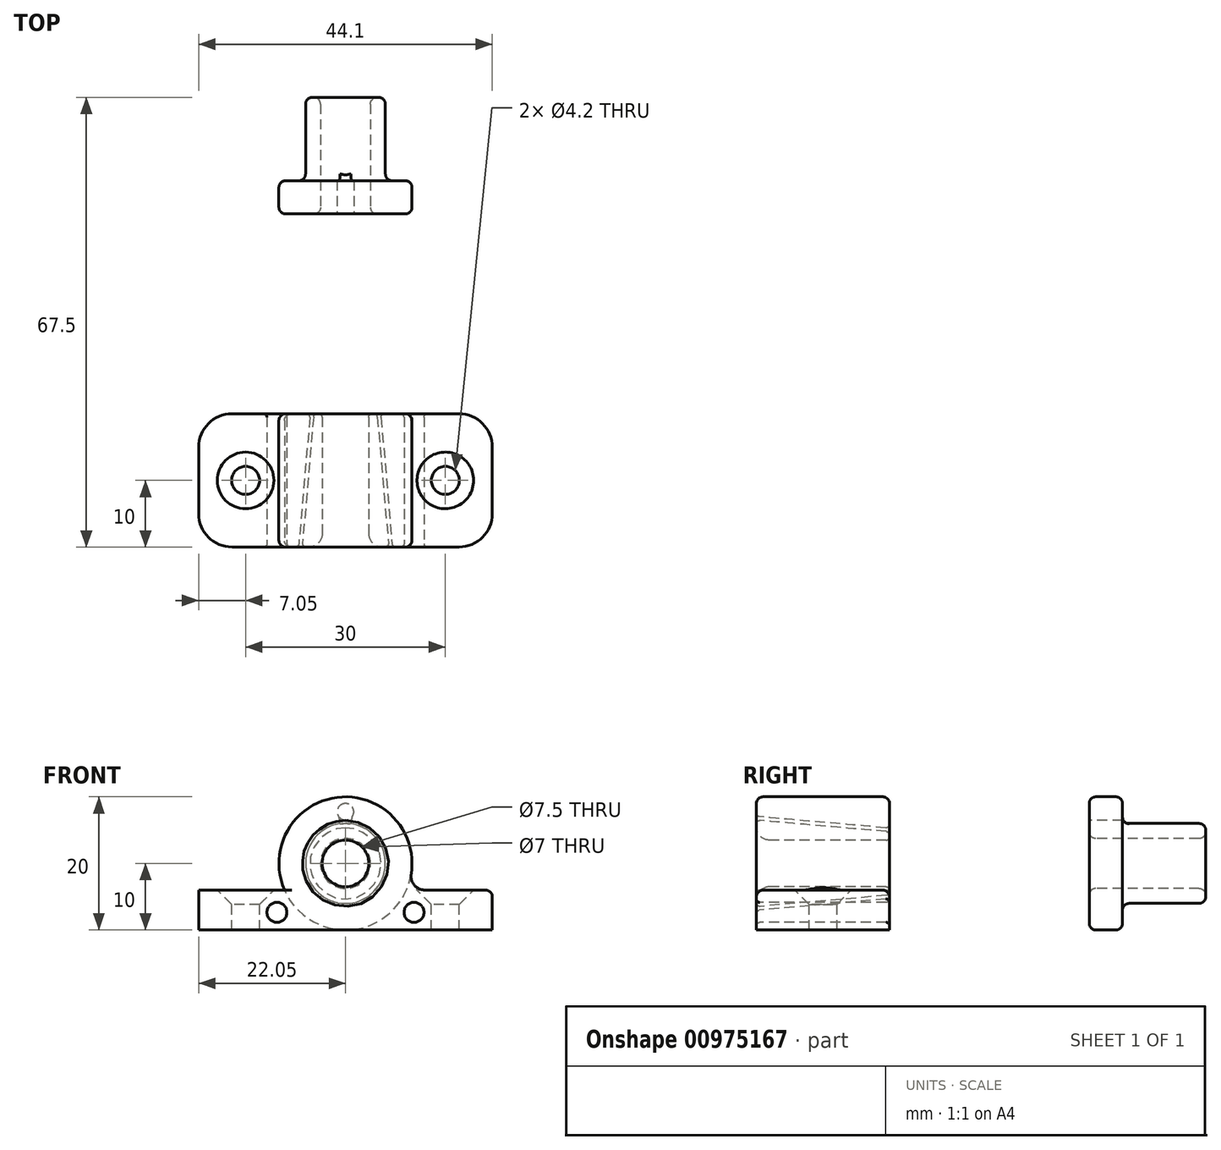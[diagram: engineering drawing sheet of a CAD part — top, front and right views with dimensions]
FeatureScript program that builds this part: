
annotation { "Feature Type Name" : "Feature", "Feature Type Description" : "" }
export const myFeature = defineFeature(function(context is Context, id is Id, definition is map)
    precondition{}
    {
        {
            var Q0;
            Q0=qCreatedBy(makeId("Right.planeOp"),FACE);
            var sketch = newSketch(context, id + "F0", { "sketchPlane" : qUnion([Q0])});
            skLineSegment(sketch, "E0", {"start": v(0, 0) * mm, "end": v(20, 0) * mm});
            skLineSegment(sketch, "E1", {"start": v(0, 3.5) * mm, "end": v(20, 3.5) * mm});
            skLineSegment(sketch, "E2", {"start": v(20, 3.5) * mm, "end": v(20, 4.75) * mm});
            skLineSegment(sketch, "E3", {"start": v(20, 4.75) * mm, "end": v(0, 6.5) * mm});
            skLineSegment(sketch, "E4", {"start": v(0, 6.5) * mm, "end": v(0, 3.5) * mm});
            skLineSegment(sketch, "E5", {"start": v(0, 7.05) * mm, "end": v(20, 5.3) * mm});
            skLineSegment(sketch, "E6", {"start": v(20, 5.3) * mm, "end": v(20, 10) * mm});
            skLineSegment(sketch, "E7", {"start": v(20, 10) * mm, "end": v(0, 10) * mm});
            skLineSegment(sketch, "E8", {"start": v(0, 10) * mm, "end": v(0, 7.05) * mm});
            skLineSegment(sketch, "E9", {"start": v(0, 3.5) * mm, "end": v(0, 0) * mm});
            skLineSegment(sketch, "E10", {"start": v(20, 3.5) * mm, "end": v(20, 0) * mm});
            skLineSegment(sketch, "E11", {"start": v(0, 7.05) * mm, "end": v(0, 6.5) * mm});
            skLineSegment(sketch, "E12", {"start": v(20, 5.3) * mm, "end": v(20, 4.75) * mm});
            skLineSegment(sketch, "E13", {"start": v(20, 5.3) * mm, "end": v(25, 5.3) * mm});
            skLineSegment(sketch, "E14", {"start": v(25, 5.3) * mm, "end": v(25, 8) * mm});
            skLineSegment(sketch, "E15", {"start": v(25, 8) * mm, "end": v(20, 8) * mm});
            skSolve(sketch);
        }
        {
            var Q0;
            Q0=qCreatedBy(makeId("Front.planeOp"),FACE);
            var sketch = newSketch(context, id + "F1", { "sketchPlane" : qUnion([Q0])});
            skPoint(sketch, "E16.0", {"position": v(0, 10) * mm});
            skPoint(sketch, "E17.0", {"position": v(0, 7.05) * mm});
            skCircle(sketch, "E18", {"center": v(0, 0) * mm, "radius": 7.05 * mm, "construction": true});
            skLineSegment(sketch, "E19.bottom", {"start": v(-22.05, -4) * mm, "end": v(-9.17, -4) * mm});
            skLineSegment(sketch, "E19.top", {"start": v(-22.05, -10) * mm, "end": v(22.05, -10) * mm});
            skLineSegment(sketch, "E19.left", {"start": v(-22.05, -4) * mm, "end": v(-22.05, -10) * mm});
            skLineSegment(sketch, "E19.right", {"start": v(22.05, -4) * mm, "end": v(22.05, -10) * mm});
            skLineSegment(sketch, "E20", {"start": v(0, 10) * mm, "end": v(0, -10) * mm, "construction": true});
            skLineSegment(sketch, "E21", {"start": v(15, -4) * mm, "end": v(15, -10) * mm, "construction": true});
            skLineSegment(sketch, "E22", {"start": v(17.05, -4) * mm, "end": v(17.05, -10) * mm, "construction": true});
            skLineSegment(sketch, "E23", {"start": v(12.95, -4) * mm, "end": v(12.95, -10) * mm, "construction": true});
            skArc(sketch, "E24", {"start": v(9.17, -4) * mm, "mid": v(0, 10) * mm, "end": v(-9.17, -4) * mm});
            skArc(sketch, "E25", {"start": v(-9.17, -4) * mm, "mid": v(0, -10) * mm, "end": v(9.17, -4) * mm, "construction": true});
            skLineSegment(sketch, "E26", {"start": v(-9.17, -4) * mm, "end": v(9.17, -4) * mm, "construction": true});
            skLineSegment(sketch, "E27", {"start": v(9.17, -4) * mm, "end": v(22.05, -4) * mm});
            skArc(sketch, "E28", {"start": v(9.88, -1.57) * mm, "mid": v(10.35, -3.26) * mm, "end": v(11.95, -4) * mm});
            skCircle(sketch, "E29", {"center": v(10.3, -7.35) * mm, "radius": 1.5 * mm});
            skLineSegment(sketch, "E30", {"start": v(11.8, -7.35) * mm, "end": v(12.95, -7.35) * mm, "construction": true});
            skLineSegment(sketch, "E31", {"start": v(10.3, -8.85) * mm, "end": v(10.3, -10) * mm, "construction": true});
            skLineSegment(sketch, "E32", {"start": v(9.08, -6.48) * mm, "end": v(8.14, -5.8) * mm, "construction": true});
            skCircle(sketch, "E33.MirrorC", {"center": v(-10.3, -7.35) * mm, "radius": 1.5 * mm});
            skArc(sketch, "E34.MirrorCS", {"start": v(-9.88, -1.57) * mm, "mid": v(-10.35, -3.26) * mm, "end": v(-11.95, -4) * mm});
            skLineSegment(sketch, "E35.MirrorCS", {"start": v(-12.95, -4) * mm, "end": v(-12.95, -10) * mm, "construction": true});
            skLineSegment(sketch, "E36.MirrorCS", {"start": v(-15, -4) * mm, "end": v(-15, -10) * mm, "construction": true});
            skLineSegment(sketch, "E37.MirrorCS", {"start": v(-17.05, -4) * mm, "end": v(-17.05, -10) * mm, "construction": true});
            skSolve(sketch);
        }
        {
            var Q0;
            Q0=qCreatedBy(makeId("Top.planeOp"),FACE);
            var sketch = newSketch(context, id + "F2", { "sketchPlane" : qUnion([Q0])});
            skPoint(sketch, "E38.0", {"position": v(15, 0) * mm});
            skLineSegment(sketch, "E39.0", {"start": v(0, 0) * mm, "end": v(0, 20) * mm, "construction": true});
            skPoint(sketch, "E40.0", {"position": v(-15, 0) * mm});
            skLineSegment(sketch, "E41", {"start": v(15, 10) * mm, "end": v(-15, 10) * mm, "construction": true});
            skPoint(sketch, "E41.startSnap0", {"position": v(0, 10) * mm});
            skSolve(sketch);
        }
        {
            var Q0;
            Q0=makeQuery(id+"F1.imprint","IMPRINT",FACE,{"disambiguationData":[TD([[makeQuery(id+"F1.imprint","IMPRINT",EDGE,{"derivedFrom":sQuery(id+"F1.wireOp",EDGE,"E19.top")}),1.0]])]});
            var Q1;
            {var subQ3=sQuery(id+"F1.wireOp",EDGE,"E28");Q1=makeQuery(id+"F1.imprint","IMPRINT",FACE,{"disambiguationData":[TD([[makeQuery(id+"F1.imprint","IMPRINT",EDGE,{"derivedFrom":subQ3}),-1.0]])]});}
            var Q2;
            {var subQ3=sQuery(id+"F1.wireOp",EDGE,"E34.MirrorCS");Q2=makeQuery(id+"F1.imprint","IMPRINT",FACE,{"disambiguationData":[TD([[makeQuery(id+"F1.imprint","IMPRINT",EDGE,{"derivedFrom":subQ3}),1.0]])]});}
            var Q3;
            Q3=sQuery(id+"F0.wireOp",VERTEX,"E6.end");
            extrude(context, id + "F3", {"entities" : qUnion([Q0, Q1, Q2]), "endBound" : BoundingType.UP_TO_VERTEX, "oppositeDirection" : true, "depth" : 25 * mm, "endBoundEntityVertex" : qUnion([Q3]), "offsetDistance" : 25 * mm});
        }
        {
            var Q0;
            Q0=makeQuery(id+"F0.imprint","IMPRINT",FACE,{"disambiguationData":[TD([[makeQuery(id+"F0.imprint","IMPRINT",EDGE,{"derivedFrom":sQuery(id+"F0.wireOp",EDGE,"E1")}),1.0]])]});
            var Q1;
            Q1=makeQuery(id+"F0.imprint","IMPRINT",FACE,{"disambiguationData":[TD([[makeQuery(id+"F0.imprint","IMPRINT",EDGE,{"derivedFrom":sQuery(id+"F0.wireOp",EDGE,"E0")}),1.0]])]});
            var Q2;
            Q2=makeQuery(id+"F0.imprint","IMPRINT",FACE,{"disambiguationData":[TD([[makeQuery(id+"F0.imprint","IMPRINT",EDGE,{"derivedFrom":sQuery(id+"F0.wireOp",EDGE,"E3")}),-1.0]])]});
            var Q3;
            Q3=sQuery(id+"F0.wireOp",EDGE,"E0");
            revolve(context, id + "F4", {"operationType" : NewBodyOperationType.REMOVE, "surfaceOperationType" : NewSurfaceOperationType.NEW, "entities" : qUnion([Q0, Q1, Q2]), "axis" : qUnion([Q3]), "revolveType" : RevolveType.FULL, "oppositeDirection" : true});
        }
        {
            var Q0;
            Q0=sQuery(id+"F2.wireOp",VERTEX,"E41.start");
            var Q1;
            Q1=sQuery(id+"F2.wireOp",VERTEX,"E41.end");
            var Q2;
            Q2=makeQuery(id+"F3.opExtrude","SWEPT_BODY",BODY,{"disambiguationData":[OSD([sQuery(id+"F1.wireOp",EDGE,"E19.bottom"),sQuery(id+"F1.wireOp",EDGE,"E19.top"),sQuery(id+"F1.wireOp",EDGE,"E19.left"),sQuery(id+"F1.wireOp",EDGE,"E19.right"),sQuery(id+"F1.wireOp",EDGE,"E24"),sQuery(id+"F1.wireOp",EDGE,"E27"),sQuery(id+"F1.wireOp",EDGE,"E28"),sQuery(id+"F1.wireOp",EDGE,"E29"),sQuery(id+"F1.wireOp",EDGE,"E33.MirrorC"),sQuery(id+"F1.wireOp",EDGE,"E34.MirrorCS")])]});
            hole(context, id + "F5", {"style" : HoleStyle.C_SINK, "endStyle" : HoleEndStyle.THROUGH, "holeDiameter" : 4.2 * mm, "cSinkDiameter" : 8.5 * mm, "cSinkAngle" : 90 * degree, "majorDiameter" : 5 * mm, "isTappedThrough" : true, "tappedDepth" : 12 * mm, "tapClearance" : 3, "locations" : qUnion([Q0, Q1]), "scope" : qUnion([Q2])});
        }
        {
            var Q0;
            Q0=makeQuery(id+"F3.opExtrude","CAP_EDGE",EDGE,{"disambiguationData":[OSD([sQuery(id+"F1.wireOp",EDGE,"E19.right")])],"isStart":true});
            var Q1;
            Q1=makeQuery(id+"F3.opExtrude","CAP_EDGE",EDGE,{"disambiguationData":[OSD([sQuery(id+"F1.wireOp",EDGE,"E19.right")])],"isStart":false});
            var Q2;
            Q2=makeQuery(id+"F3.opExtrude","CAP_EDGE",EDGE,{"disambiguationData":[OSD([sQuery(id+"F1.wireOp",EDGE,"E19.left")])],"isStart":true});
            var Q3;
            Q3=makeQuery(id+"F3.opExtrude","CAP_EDGE",EDGE,{"disambiguationData":[OSD([sQuery(id+"F1.wireOp",EDGE,"E19.left")])],"isStart":false});
            fillet(context, id + "F6", {"entities" : qUnion([Q0, Q1, Q2, Q3]), "radius" : 5 * mm, "tangentPropagation" : true, "allowEdgeOverflow" : false});
        }
        {
            var Q0;
            Q0=makeQuery(id+"F3.opExtrude","CAP_EDGE",EDGE,{"disambiguationData":[OSD([sQuery(id+"F1.wireOp",EDGE,"E24")])],"isStart":true});
            fillet(context, id + "F7", {"entities" : qUnion([Q0]), "radius" : 1 * mm, "tangentPropagation" : true, "allowEdgeOverflow" : false});
        }
        {
            var Q0;
            Q0=makeQuery(id+"F4.boolean.opBoolean","COPY",EDGE,{"derivedFrom":makeQuery(id+"F4.opRevolve","SWEPT_EDGE",EDGE,{"disambiguationData":[OSD([sQuery(id+"F0.wireOp",EDGE,"E5"),sQuery(id+"F0.wireOp",EDGE,"E8"),sQuery(id+"F0.wireOp",EDGE,"E11")])]})});
            var Q1;
            Q1=makeQuery(id+"F3.opExtrude","CAP_EDGE",EDGE,{"disambiguationData":[OSD([sQuery(id+"F1.wireOp",EDGE,"E33.MirrorC")])],"isStart":true});
            var Q2;
            Q2=makeQuery(id+"F3.opExtrude","CAP_EDGE",EDGE,{"disambiguationData":[OSD([sQuery(id+"F1.wireOp",EDGE,"E29")])],"isStart":true});
            var Q3;
            Q3=makeQuery(id+"F3.opExtrude","CAP_EDGE",EDGE,{"disambiguationData":[OSD([sQuery(id+"F1.wireOp",EDGE,"E29")])],"isStart":false});
            var Q4;
            Q4=makeQuery(id+"F4.boolean.opBoolean","COPY",FACE,{"derivedFrom":makeQuery(id+"F4.opRevolve","SWEPT_FACE",FACE,{"disambiguationData":[OSD([sQuery(id+"F0.wireOp",EDGE,"E5")])]})});
            var Q5;
            Q5=makeQuery(id+"F3.opExtrude","CAP_EDGE",EDGE,{"disambiguationData":[OSD([sQuery(id+"F1.wireOp",EDGE,"E33.MirrorC")])],"isStart":false});
            var Q6;
            Q6=makeQuery(id+"FBThXqd1cxYpDcm_1.opRevolve","SWEPT_EDGE",EDGE,{"disambiguationData":[OSD([sQuery(id+"F0.wireOp",EDGE,"E13"),sQuery(id+"F0.wireOp",EDGE,"E14")])]});
            var Q7;
            Q7=makeQuery(id+"FBThXqd1cxYpDcm_1.opRevolve","SWEPT_EDGE",EDGE,{"disambiguationData":[OSD([sQuery(id+"F0.wireOp",EDGE,"E14"),sQuery(id+"F0.wireOp",EDGE,"E15")])]});
            fillet(context, id + "F8", {"entities" : qUnion([Q0, Q1, Q2, Q3, Q4, Q5, Q6, Q7]), "radius" : .5 * mm, "tangentPropagation" : true, "allowEdgeOverflow" : false});
        }
        {
            var Q0;
            Q0=makeQuery(id+"F0.imprint","IMPRINT",FACE,{"disambiguationData":[TD([[makeQuery(id+"F0.imprint","IMPRINT",EDGE,{"derivedFrom":sQuery(id+"F0.wireOp",EDGE,"E1")}),1.0]])]});
            var Q1;
            Q1=sQuery(id+"F0.wireOp",EDGE,"E0");
            revolve(context, id + "F9", {"surfaceOperationType" : NewSurfaceOperationType.NEW, "entities" : qUnion([Q0]), "axis" : qUnion([Q1]), "revolveType" : RevolveType.FULL});
        }
        {
            var Q0;
            Q0=makeQuery(id+"F9.opRevolve","SWEPT_EDGE",EDGE,{"disambiguationData":[OSD([sQuery(id+"F0.wireOp",EDGE,"E1"),sQuery(id+"F0.wireOp",EDGE,"E4"),sQuery(id+"F0.wireOp",EDGE,"E9")])]});
            fillet(context, id + "F10", {"entities" : qUnion([Q0]), "radius" : 2 * mm, "tangentPropagation" : true, "allowEdgeOverflow" : false});
        }
        {
            var Q0;
            Q0=makeQuery(id+"F9.opRevolve","SWEPT_FACE",FACE,{"disambiguationData":[OSD([sQuery(id+"F0.wireOp",EDGE,"E3")])]});
            var Q1;
            Q1=makeQuery(id+"F9.opRevolve","SWEPT_EDGE",EDGE,{"disambiguationData":[OSD([sQuery(id+"F0.wireOp",EDGE,"E1"),sQuery(id+"F0.wireOp",EDGE,"E2"),sQuery(id+"F0.wireOp",EDGE,"E10")])]});
            fillet(context, id + "F11", {"entities" : qUnion([Q0, Q1]), "radius" : .5 * mm, "tangentPropagation" : true, "allowEdgeOverflow" : false});
        }
        {
            var Q0;
            Q0=qCreatedBy(makeId("Right.planeOp"),FACE);
            var sketch = newSketch(context, id + "F12", { "sketchPlane" : qUnion([Q0])});
            skPoint(sketch, "E42.0", {"position": v(20, 10) * mm});
            skPoint(sketch, "E43.0", {"position": v(20, 3.5) * mm});
            skLineSegment(sketch, "E44", {"start": v(50, 10) * mm, "end": v(50, 3.75) * mm});
            skLineSegment(sketch, "E45", {"start": v(50, 10) * mm, "end": v(55, 10) * mm});
            skLineSegment(sketch, "E46", {"start": v(55, 10) * mm, "end": v(55, 6) * mm});
            skLineSegment(sketch, "E47", {"start": v(55, 6) * mm, "end": v(67.5, 6) * mm});
            skLineSegment(sketch, "E48", {"start": v(67.5, 6) * mm, "end": v(67.5, 3.75) * mm});
            skLineSegment(sketch, "E49", {"start": v(67.5, 3.75) * mm, "end": v(50, 3.75) * mm});
            skLineSegment(sketch, "E50", {"start": v(50, 9) * mm, "end": v(55, 9) * mm, "construction": true});
            skLineSegment(sketch, "E51", {"start": v(50, 7.75) * mm, "end": v(55, 7.75) * mm, "construction": true});
            skLineSegment(sketch, "E52", {"start": v(50, 6.5) * mm, "end": v(55, 6.5) * mm, "construction": true});
            skLineSegment(sketch, "E53", {"start": v(50, 0) * mm, "end": v(67.5, 0) * mm, "construction": true});
            skSolve(sketch);
        }
        {
            var Q0;
            Q0=qCreatedBy(makeId("Front.planeOp"),FACE);
            var Q1;
            Q1=sQuery(id+"F12.wireOp",VERTEX,"E44.end");
            cPlane(context, id + "F13", {"entities" : qUnion([Q0, Q1]), "cplaneType" : CPlaneType.PLANE_POINT, "offset" : 25 * mm, "width" : 150 * mm, "height" : 150 * mm});
        }
        {
            var Q0;
            Q0=qCreatedBy(id+"F13.planeOp",FACE);
            var sketch = newSketch(context, id + "F14", { "sketchPlane" : qUnion([Q0])});
            skPoint(sketch, "E54.0", {"position": v(0, 0) * mm});
            skPoint(sketch, "E55.0", {"position": v(0, 7.75) * mm});
            skPoint(sketch, "E56.0", {"position": v(0, 9) * mm});
            skCircle(sketch, "E57", {"center": v(0, 7.75) * mm, "radius": 1.25 * mm});
            skLineSegment(sketch, "E58", {"start": v(0, 0) * mm, "end": v(4.05, 0) * mm, "construction": true});
            skCircle(sketch, "E59.MirrorC", {"center": v(0, -7.75) * mm, "radius": 1.25 * mm});
            skSolve(sketch);
        }
        {
            var Q0;
            Q0=makeQuery(id+"F12.imprint","IMPRINT",FACE,{"disambiguationData":[TD([[makeQuery(id+"F12.imprint","IMPRINT",EDGE,{"derivedFrom":sQuery(id+"F12.wireOp",EDGE,"E44")}),1.0]])]});
            var Q1;
            Q1=sQuery(id+"F12.wireOp",EDGE,"E53");
            revolve(context, id + "F15", {"surfaceOperationType" : NewSurfaceOperationType.NEW, "entities" : qUnion([Q0]), "axis" : qUnion([Q1]), "revolveType" : RevolveType.FULL});
        }
        {
            var Q0;
            Q0=makeQuery(id+"F14.imprint","IMPRINT",FACE,{"disambiguationData":[TD([[makeQuery(id+"F14.imprint","IMPRINT",EDGE,{"derivedFrom":sQuery(id+"F14.wireOp",EDGE,"E59.MirrorC")}),-1.0]])]});
            var Q1;
            Q1=makeQuery(id+"F14.imprint","IMPRINT",FACE,{"disambiguationData":[TD([[makeQuery(id+"F14.imprint","IMPRINT",EDGE,{"derivedFrom":sQuery(id+"F14.wireOp",EDGE,"E57")}),1.0]])]});
            extrude(context, id + "F16", {"entities" : qUnion([Q0, Q1]), "operationType" : NewBodyOperationType.REMOVE, "endBound" : BoundingType.THROUGH_ALL, "oppositeDirection" : true, "depth" : 25 * mm, "offsetDistance" : 25 * mm});
        }
        {
            var Q0;
            Q0=makeQuery(id+"F15.opRevolve","SWEPT_EDGE",EDGE,{"disambiguationData":[OSD([sQuery(id+"F12.wireOp",EDGE,"E44"),sQuery(id+"F12.wireOp",EDGE,"E49")])]});
            var Q1;
            Q1=makeQuery(id+"F15.opRevolve","SWEPT_FACE",FACE,{"disambiguationData":[OSD([sQuery(id+"F12.wireOp",EDGE,"E48")])]});
            var Q2;
            Q2=makeQuery(id+"F15.opRevolve","SWEPT_EDGE",EDGE,{"disambiguationData":[OSD([sQuery(id+"F12.wireOp",EDGE,"E45"),sQuery(id+"F12.wireOp",EDGE,"E46")])]});
            var Q3;
            Q3=makeQuery(id+"F15.opRevolve","SWEPT_EDGE",EDGE,{"disambiguationData":[OSD([sQuery(id+"F12.wireOp",EDGE,"E46"),sQuery(id+"F12.wireOp",EDGE,"E47")])]});
            var Q4;
            Q4=makeQuery(id+"F15.opRevolve","SWEPT_EDGE",EDGE,{"disambiguationData":[OSD([sQuery(id+"F12.wireOp",EDGE,"E44"),sQuery(id+"F12.wireOp",EDGE,"E45")])]});
            fillet(context, id + "F17", {"entities" : qUnion([Q0, Q1, Q2, Q3, Q4]), "radius" : 1 * mm, "tangentPropagation" : true, "allowEdgeOverflow" : false});
        }
    });
